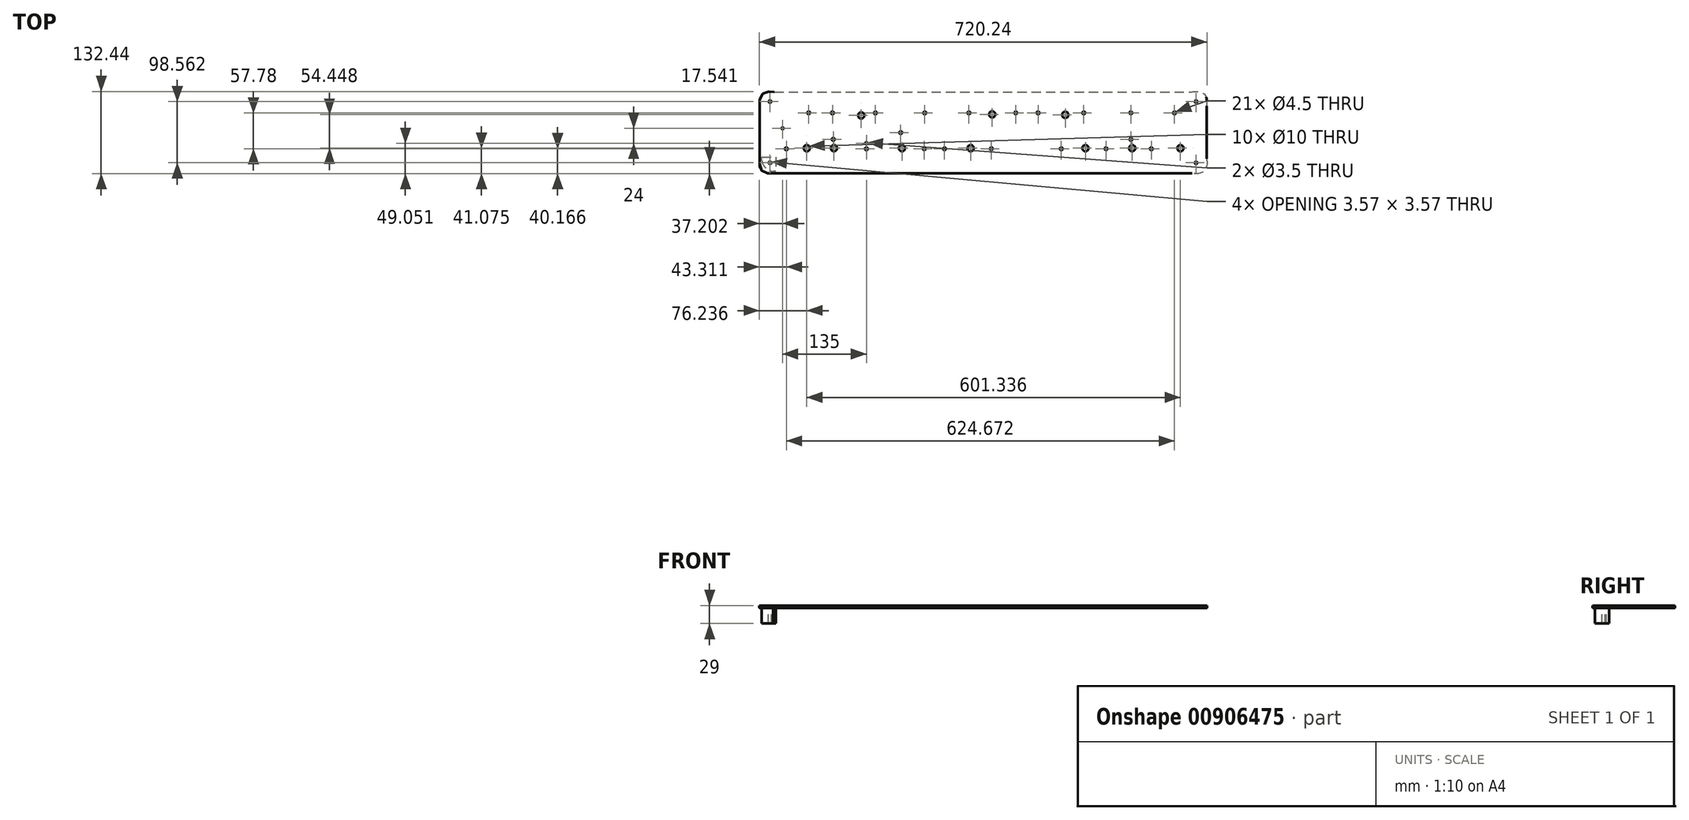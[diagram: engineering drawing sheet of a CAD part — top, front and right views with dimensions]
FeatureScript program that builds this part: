
annotation { "Feature Type Name" : "Feature", "Feature Type Description" : "" }
export const myFeature = defineFeature(function(context is Context, id is Id, definition is map)
    precondition{}
    {
        {
            var Q0;
            Q0=qCreatedBy(makeId("Top.planeOp"),FACE);
            var sketch = newSketch(context, id + "F0", { "sketchPlane" : qUnion([Q0])});
            skFitSpline(sketch, "E0", {"points": [v(336.08, -65.5) * mm, v(336.08, -65.5) * mm, v(336.08, -65.5) * mm, v(333.9, -65.5) * mm, v(-335.86, -65.5) * mm, v(-336.08, -65.5) * mm, v(-336.08, -65.5) * mm, v(-349.03, -65.5) * mm, v(-359.52, -55) * mm, v(-359.52, -42.07) * mm, v(-359.52, -42.06) * mm, v(-359.52, -42.04) * mm, v(-359.52, 42.04) * mm, v(-359.52, 42.06) * mm, v(-359.52, 42.07) * mm, v(-359.51, 55.02) * mm, v(-349.02, 65.5) * mm, v(-336.08, 65.5) * mm]});
            skFitSpline(sketch, "E1", {"points": [v(-336.08, 65.5) * mm, v(-336.08, 65.5) * mm, v(-336.08, 65.5) * mm, v(-333.9, 65.5) * mm, v(335.86, 65.5) * mm, v(336.08, 65.5) * mm, v(336.08, 65.5) * mm, v(349.03, 65.5) * mm, v(359.52, 55) * mm, v(359.52, 42.07) * mm, v(359.52, 42.06) * mm, v(359.52, 42.04) * mm, v(359.52, -42.04) * mm, v(359.52, -42.06) * mm, v(359.52, -42.07) * mm, v(359.51, -55.02) * mm, v(349.02, -65.5) * mm, v(336.08, -65.5) * mm]});
            skFitSpline(sketch, "E2", {"points": [v(-341.32, 49.88) * mm, v(-341.32, 48.9) * mm, v(-342.12, 48.1) * mm, v(-343.1, 48.1) * mm, v(-344.09, 48.1) * mm, v(-344.89, 48.9) * mm, v(-344.89, 49.88) * mm, v(-344.89, 50.87) * mm, v(-344.09, 51.67) * mm, v(-343.1, 51.67) * mm, v(-342.12, 51.67) * mm, v(-341.32, 50.87) * mm, v(-341.32, 49.88) * mm]});
            skFitSpline(sketch, "E3", {"points": [v(-341.32, -48.68) * mm, v(-341.32, -49.66) * mm, v(-342.12, -50.46) * mm, v(-343.1, -50.46) * mm, v(-344.09, -50.46) * mm, v(-344.89, -49.66) * mm, v(-344.89, -48.68) * mm, v(-344.89, -47.7) * mm, v(-344.09, -46.9) * mm, v(-343.1, -46.9) * mm, v(-342.12, -46.9) * mm, v(-341.32, -47.7) * mm, v(-341.32, -48.68) * mm]});
            skFitSpline(sketch, "E4", {"points": [v(344.46, 49.88) * mm, v(344.46, 48.9) * mm, v(343.66, 48.1) * mm, v(342.67, 48.1) * mm, v(341.69, 48.1) * mm, v(340.89, 48.9) * mm, v(340.89, 49.88) * mm, v(340.89, 50.87) * mm, v(341.69, 51.67) * mm, v(342.67, 51.67) * mm, v(343.66, 51.67) * mm, v(344.46, 50.87) * mm, v(344.46, 49.88) * mm]});
            skFitSpline(sketch, "E5", {"points": [v(344.46, -48.68) * mm, v(344.46, -49.66) * mm, v(343.66, -50.46) * mm, v(342.67, -50.46) * mm, v(341.69, -50.46) * mm, v(340.89, -49.66) * mm, v(340.89, -48.68) * mm, v(340.89, -47.7) * mm, v(341.69, -46.9) * mm, v(342.67, -46.9) * mm, v(343.66, -46.9) * mm, v(344.46, -47.7) * mm, v(344.46, -48.68) * mm]});
            skCircle(sketch, "E6", {"center": v(-283.88, -25.14) * mm, "radius": 5 * mm});
            skCircle(sketch, "E7", {"center": v(-240.2, -25.14) * mm, "radius": 5 * mm});
            skCircle(sketch, "E8", {"center": v(-20.1, -25.14) * mm, "radius": 5 * mm});
            skCircle(sketch, "E9", {"center": v(164.53, -25.14) * mm, "radius": 5 * mm});
            skCircle(sketch, "E10", {"center": v(239.74, -25.14) * mm, "radius": 5 * mm});
            skCircle(sketch, "E11", {"center": v(-196.36, 27.6) * mm, "radius": 5 * mm});
            skCircle(sketch, "E12", {"center": v(-130.77, -25.14) * mm, "radius": 5 * mm});
            skCircle(sketch, "E13", {"center": v(14.5, 29.3) * mm, "radius": 5 * mm});
            skCircle(sketch, "E14", {"center": v(132.07, 28.46) * mm, "radius": 5 * mm});
            skCircle(sketch, "E15", {"center": v(317.45, -25.14) * mm, "radius": 5 * mm});
            skSolve(sketch);
        }
        {
            var Q0;
            Q0=qCreatedBy(makeId("Top.planeOp"),FACE);
            var sketch = newSketch(context, id + "F1", { "sketchPlane" : qUnion([Q0])});
            skLineSegment(sketch, "E16", {"start": v(-330.73, -38.95) * mm, "end": v(-330.73, 5.14) * mm});
            skLineSegment(sketch, "E17", {"start": v(-330.73, 5.14) * mm, "end": v(-293.42, 5.14) * mm});
            skLineSegment(sketch, "E18", {"start": v(-293.42, 5.14) * mm, "end": v(-293.42, -11.79) * mm});
            skLineSegment(sketch, "E19", {"start": v(-293.42, -11.79) * mm, "end": v(-296.81, -15.18) * mm});
            skLineSegment(sketch, "E20", {"start": v(-296.81, -15.18) * mm, "end": v(-296.81, -18.63) * mm});
            skLineSegment(sketch, "E21", {"start": v(-296.81, -18.63) * mm, "end": v(-293.42, -22) * mm});
            skLineSegment(sketch, "E22", {"start": v(-293.42, -22) * mm, "end": v(-293.42, -38.95) * mm});
            skLineSegment(sketch, "E23", {"start": v(-293.42, -38.95) * mm, "end": v(-330.73, -38.95) * mm});
            skLineSegment(sketch, "E24", {"start": v(-317.16, -5.03) * mm, "end": v(-317.16, -11.82) * mm});
            skLineSegment(sketch, "E25", {"start": v(-317.16, -11.82) * mm, "end": v(-313.83, -11.82) * mm});
            skLineSegment(sketch, "E26", {"start": v(-313.83, -11.82) * mm, "end": v(-310.37, -8.58) * mm});
            skLineSegment(sketch, "E27", {"start": v(-310.37, -8.58) * mm, "end": v(-310.37, -5.03) * mm});
            skLineSegment(sketch, "E28", {"start": v(-310.37, -5.03) * mm, "end": v(-313.86, -5.03) * mm});
            skLineSegment(sketch, "E29", {"start": v(-313.86, -5.03) * mm, "end": v(-317.16, -5.03) * mm});
            skLineSegment(sketch, "E30", {"start": v(-317.16, -22) * mm, "end": v(-317.16, -28.78) * mm});
            skLineSegment(sketch, "E31", {"start": v(-317.16, -28.78) * mm, "end": v(-313.81, -28.78) * mm});
            skLineSegment(sketch, "E32", {"start": v(-313.81, -28.78) * mm, "end": v(-310.37, -25.37) * mm});
            skLineSegment(sketch, "E33", {"start": v(-310.37, -25.37) * mm, "end": v(-310.37, -22) * mm});
            skLineSegment(sketch, "E34", {"start": v(-310.37, -22) * mm, "end": v(-313.74, -22) * mm});
            skLineSegment(sketch, "E35", {"start": v(-313.74, -22) * mm, "end": v(-317.16, -22) * mm});
            skLineSegment(sketch, "E36", {"start": v(-289.9, 5.14) * mm, "end": v(-272.94, 5.14) * mm});
            skLineSegment(sketch, "E37", {"start": v(-272.94, 5.14) * mm, "end": v(-272.94, -38.95) * mm});
            skLineSegment(sketch, "E38", {"start": v(-272.94, -38.95) * mm, "end": v(-289.9, -38.95) * mm});
            skLineSegment(sketch, "E39", {"start": v(-289.9, -38.95) * mm, "end": v(-289.9, 5.14) * mm});
            skLineSegment(sketch, "E40", {"start": v(-259.27, -38.95) * mm, "end": v(-259.27, -15.2) * mm});
            skLineSegment(sketch, "E41", {"start": v(-259.27, -15.2) * mm, "end": v(-269.43, -15.2) * mm});
            skLineSegment(sketch, "E42", {"start": v(-269.43, -15.2) * mm, "end": v(-269.43, 5.14) * mm});
            skLineSegment(sketch, "E43", {"start": v(-269.43, 5.14) * mm, "end": v(-232.12, 5.14) * mm});
            skLineSegment(sketch, "E44", {"start": v(-232.12, 5.14) * mm, "end": v(-232.12, -15.2) * mm});
            skLineSegment(sketch, "E45", {"start": v(-232.12, -15.2) * mm, "end": v(-242.28, -15.2) * mm});
            skLineSegment(sketch, "E46", {"start": v(-242.28, -15.2) * mm, "end": v(-242.28, -38.95) * mm});
            skLineSegment(sketch, "E47", {"start": v(-242.28, -38.95) * mm, "end": v(-259.27, -38.95) * mm});
            skLineSegment(sketch, "E48", {"start": v(-228.6, -38.95) * mm, "end": v(-228.6, 5.14) * mm});
            skLineSegment(sketch, "E49", {"start": v(-228.6, 5.14) * mm, "end": v(-191.3, 5.14) * mm});
            skLineSegment(sketch, "E50", {"start": v(-191.3, 5.14) * mm, "end": v(-191.3, -18.6) * mm});
            skLineSegment(sketch, "E51", {"start": v(-191.3, -18.6) * mm, "end": v(-194.73, -22) * mm});
            skLineSegment(sketch, "E52", {"start": v(-194.73, -22) * mm, "end": v(-191.3, -25.39) * mm});
            skLineSegment(sketch, "E53", {"start": v(-191.3, -25.39) * mm, "end": v(-191.3, -38.95) * mm});
            skLineSegment(sketch, "E54", {"start": v(-191.3, -38.95) * mm, "end": v(-208.28, -38.95) * mm});
            skLineSegment(sketch, "E55", {"start": v(-208.28, -38.95) * mm, "end": v(-208.28, -22.04) * mm});
            skLineSegment(sketch, "E56", {"start": v(-208.28, -22.04) * mm, "end": v(-211.67, -22.04) * mm});
            skLineSegment(sketch, "E57", {"start": v(-211.67, -22.04) * mm, "end": v(-211.67, -38.95) * mm});
            skLineSegment(sketch, "E58", {"start": v(-211.67, -38.95) * mm, "end": v(-228.6, -38.95) * mm});
            skLineSegment(sketch, "E59", {"start": v(-215.06, -5.03) * mm, "end": v(-215.06, -11.82) * mm});
            skLineSegment(sketch, "E60", {"start": v(-215.06, -11.82) * mm, "end": v(-211.71, -11.82) * mm});
            skLineSegment(sketch, "E61", {"start": v(-211.71, -11.82) * mm, "end": v(-208.28, -8.41) * mm});
            skLineSegment(sketch, "E62", {"start": v(-208.28, -8.41) * mm, "end": v(-208.28, -5.03) * mm});
            skLineSegment(sketch, "E63", {"start": v(-208.28, -5.03) * mm, "end": v(-211.64, -5.03) * mm});
            skLineSegment(sketch, "E64", {"start": v(-211.64, -5.03) * mm, "end": v(-215.06, -5.03) * mm});
            skLineSegment(sketch, "E65", {"start": v(-187.79, -38.95) * mm, "end": v(-187.79, 5.14) * mm});
            skLineSegment(sketch, "E66", {"start": v(-187.79, 5.14) * mm, "end": v(-150.47, 5.14) * mm});
            skLineSegment(sketch, "E67", {"start": v(-150.47, 5.14) * mm, "end": v(-150.47, -38.95) * mm});
            skLineSegment(sketch, "E68", {"start": v(-150.47, -38.95) * mm, "end": v(-187.79, -38.95) * mm});
            skLineSegment(sketch, "E69", {"start": v(-174.17, -5.15) * mm, "end": v(-174.17, -25.5) * mm});
            skLineSegment(sketch, "E70", {"start": v(-174.17, -25.5) * mm, "end": v(-167.39, -25.5) * mm});
            skLineSegment(sketch, "E71", {"start": v(-167.39, -25.5) * mm, "end": v(-167.39, -5.15) * mm});
            skLineSegment(sketch, "E72", {"start": v(-167.39, -5.15) * mm, "end": v(-174.17, -5.15) * mm});
            skLineSegment(sketch, "E73", {"start": v(-146.96, -38.95) * mm, "end": v(-146.96, 5.14) * mm});
            skLineSegment(sketch, "E74", {"start": v(-146.96, 5.14) * mm, "end": v(-109.65, 5.14) * mm});
            skLineSegment(sketch, "E75", {"start": v(-109.65, 5.14) * mm, "end": v(-109.65, -18.83) * mm});
            skLineSegment(sketch, "E76", {"start": v(-109.65, -18.83) * mm, "end": v(-112.94, -22.03) * mm});
            skLineSegment(sketch, "E77", {"start": v(-112.94, -22.03) * mm, "end": v(-123.2, -22.03) * mm});
            skLineSegment(sketch, "E78", {"start": v(-123.2, -22.03) * mm, "end": v(-123.2, -38.95) * mm});
            skLineSegment(sketch, "E79", {"start": v(-123.2, -38.95) * mm, "end": v(-146.96, -38.95) * mm});
            skLineSegment(sketch, "E80", {"start": v(-133.4, -5.03) * mm, "end": v(-133.4, -11.82) * mm});
            skLineSegment(sketch, "E81", {"start": v(-133.4, -11.82) * mm, "end": v(-130.05, -11.82) * mm});
            skLineSegment(sketch, "E82", {"start": v(-130.05, -11.82) * mm, "end": v(-126.62, -8.41) * mm});
            skLineSegment(sketch, "E83", {"start": v(-126.62, -8.41) * mm, "end": v(-126.62, -5.03) * mm});
            skLineSegment(sketch, "E84", {"start": v(-126.62, -5.03) * mm, "end": v(-129.98, -5.03) * mm});
            skLineSegment(sketch, "E85", {"start": v(-129.98, -5.03) * mm, "end": v(-133.4, -5.03) * mm});
            skLineSegment(sketch, "E86", {"start": v(-106.14, -38.95) * mm, "end": v(-106.14, 5.14) * mm});
            skLineSegment(sketch, "E87", {"start": v(-106.14, 5.14) * mm, "end": v(-68.83, 5.14) * mm});
            skLineSegment(sketch, "E88", {"start": v(-68.83, 5.14) * mm, "end": v(-68.83, -38.95) * mm});
            skLineSegment(sketch, "E89", {"start": v(-68.83, -38.95) * mm, "end": v(-106.14, -38.95) * mm});
            skLineSegment(sketch, "E90", {"start": v(-92.57, -5.15) * mm, "end": v(-92.57, -25.5) * mm});
            skLineSegment(sketch, "E91", {"start": v(-92.57, -25.5) * mm, "end": v(-85.79, -25.5) * mm});
            skLineSegment(sketch, "E92", {"start": v(-85.79, -25.5) * mm, "end": v(-85.79, -5.15) * mm});
            skLineSegment(sketch, "E93", {"start": v(-85.79, -5.15) * mm, "end": v(-92.57, -5.15) * mm});
            skLineSegment(sketch, "E94", {"start": v(-65.32, -38.95) * mm, "end": v(-65.32, 5.14) * mm});
            skLineSegment(sketch, "E95", {"start": v(-65.32, 5.14) * mm, "end": v(-48.24, 5.14) * mm});
            skLineSegment(sketch, "E96", {"start": v(-48.24, 5.14) * mm, "end": v(-48.24, -25.4) * mm});
            skLineSegment(sketch, "E97", {"start": v(-48.24, -25.4) * mm, "end": v(-28, -25.4) * mm});
            skLineSegment(sketch, "E98", {"start": v(-28, -25.4) * mm, "end": v(-28, -38.95) * mm});
            skLineSegment(sketch, "E99", {"start": v(-28, -38.95) * mm, "end": v(-65.32, -38.95) * mm});
            skLineSegment(sketch, "E100", {"start": v(-24.5, 5.14) * mm, "end": v(-7.53, 5.14) * mm});
            skLineSegment(sketch, "E101", {"start": v(-7.53, 5.14) * mm, "end": v(-7.53, -38.95) * mm});
            skLineSegment(sketch, "E102", {"start": v(-7.53, -38.95) * mm, "end": v(-24.5, -38.95) * mm});
            skLineSegment(sketch, "E103", {"start": v(-24.5, -38.95) * mm, "end": v(-24.5, 5.14) * mm});
            skLineSegment(sketch, "E104", {"start": v(-4.02, -38.95) * mm, "end": v(-4.02, -25.4) * mm});
            skLineSegment(sketch, "E105", {"start": v(-4.02, -25.4) * mm, "end": v(19.67, -25.4) * mm});
            skLineSegment(sketch, "E106", {"start": v(19.67, -25.4) * mm, "end": v(19.67, -22.03) * mm});
            skLineSegment(sketch, "E107", {"start": v(19.67, -22.03) * mm, "end": v(-4.02, -22.03) * mm});
            skLineSegment(sketch, "E108", {"start": v(-4.02, -22.03) * mm, "end": v(-4.02, 5.14) * mm});
            skLineSegment(sketch, "E109", {"start": v(-4.02, 5.14) * mm, "end": v(33.29, 5.14) * mm});
            skLineSegment(sketch, "E110", {"start": v(33.29, 5.14) * mm, "end": v(33.29, -8.43) * mm});
            skLineSegment(sketch, "E111", {"start": v(33.29, -8.43) * mm, "end": v(9.54, -8.43) * mm});
            skLineSegment(sketch, "E112", {"start": v(9.54, -8.43) * mm, "end": v(9.54, -11.82) * mm});
            skLineSegment(sketch, "E113", {"start": v(9.54, -11.82) * mm, "end": v(33.29, -11.82) * mm});
            skLineSegment(sketch, "E114", {"start": v(33.29, -11.82) * mm, "end": v(33.29, -38.95) * mm});
            skLineSegment(sketch, "E115", {"start": v(33.29, -38.95) * mm, "end": v(-4.02, -38.95) * mm});
            skFitSpline(sketch, "E116", {"points": [v(36.9, -53.5) * mm, v(36.89, -53.5) * mm, v(36.89, -53.5) * mm, v(35.69, -53.5) * mm, v(-333.72, -53.5) * mm, v(-333.84, -53.5) * mm, v(-333.84, -53.5) * mm, v(-340.98, -53.5) * mm, v(-346.77, -47.71) * mm, v(-346.77, -40.57) * mm, v(-346.77, -40.57) * mm, v(-346.77, -40.56) * mm, v(-346.77, 5.82) * mm, v(-346.77, 5.83) * mm, v(-346.77, 5.83) * mm, v(-346.76, 12.97) * mm, v(-340.98, 18.76) * mm, v(-333.84, 18.76) * mm]});
            skFitSpline(sketch, "E117", {"points": [v(-333.84, 18.76) * mm, v(-333.84, 18.76) * mm, v(-333.84, 18.76) * mm, v(-332.63, 18.76) * mm, v(36.77, 18.76) * mm, v(36.9, 18.76) * mm, v(36.9, 18.76) * mm, v(44.03, 18.75) * mm, v(49.82, 12.97) * mm, v(49.82, 5.83) * mm, v(49.82, 5.83) * mm, v(49.82, 5.81) * mm, v(49.82, -40.56) * mm, v(49.82, -40.57) * mm, v(49.82, -40.58) * mm, v(49.82, -47.72) * mm, v(44.03, -53.5) * mm, v(36.9, -53.5) * mm]});
            skFitSpline(sketch, "E118", {"points": [v(-336.73, 10.14) * mm, v(-336.73, 9.6) * mm, v(-337.17, 9.16) * mm, v(-337.71, 9.16) * mm, v(-338.26, 9.16) * mm, v(-338.7, 9.6) * mm, v(-338.7, 10.14) * mm, v(-338.7, 10.68) * mm, v(-338.26, 11.13) * mm, v(-337.71, 11.13) * mm, v(-337.17, 11.13) * mm, v(-336.73, 10.68) * mm, v(-336.73, 10.14) * mm]});
            skFitSpline(sketch, "E119", {"points": [v(-336.73, -44.22) * mm, v(-336.73, -44.76) * mm, v(-337.17, -45.2) * mm, v(-337.71, -45.2) * mm, v(-338.26, -45.2) * mm, v(-338.7, -44.76) * mm, v(-338.7, -44.22) * mm, v(-338.7, -43.68) * mm, v(-338.26, -43.24) * mm, v(-337.71, -43.24) * mm, v(-337.17, -43.24) * mm, v(-336.73, -43.68) * mm, v(-336.73, -44.22) * mm]});
            skFitSpline(sketch, "E120", {"points": [v(41.51, 10.14) * mm, v(41.51, 9.6) * mm, v(41.07, 9.16) * mm, v(40.53, 9.16) * mm, v(39.98, 9.16) * mm, v(39.54, 9.6) * mm, v(39.54, 10.14) * mm, v(39.54, 10.68) * mm, v(39.98, 11.13) * mm, v(40.53, 11.13) * mm, v(41.07, 11.13) * mm, v(41.51, 10.68) * mm, v(41.51, 10.14) * mm]});
            skFitSpline(sketch, "E121", {"points": [v(41.51, -44.22) * mm, v(41.51, -44.76) * mm, v(41.07, -45.2) * mm, v(40.53, -45.2) * mm, v(39.98, -45.2) * mm, v(39.54, -44.76) * mm, v(39.54, -44.22) * mm, v(39.54, -43.68) * mm, v(39.98, -43.24) * mm, v(40.53, -43.24) * mm, v(41.07, -43.24) * mm, v(41.51, -43.68) * mm, v(41.51, -44.22) * mm]});
            skSolve(sketch);
        }
        {
            var Q0;
            Q0 = qConstructionFilter(qBodyType(qCreatedBy(id + "F1" ,EDGE), BodyType.WIRE), ConstructionObject.NO);
            extrude(context, id + "F2", {"bodyType" : ToolBodyType.SURFACE, "surfaceEntities" : qUnion([Q0]), "depth" : 25 * mm, "offsetDistance" : 25 * mm});
        }
        {
            var Q0;
            Q0=makeQuery(id+"F2.opExtrude","SWEPT_BODY",BODY,{"disambiguationData":[OSD([sQuery(id+"F1.wireOp",EDGE,"E23")])]});
            var Q1;
            Q1=makeQuery(id+"F2.opExtrude","SWEPT_BODY",BODY,{"disambiguationData":[OSD([sQuery(id+"F1.wireOp",EDGE,"E28"),sQuery(id+"F1.wireOp",EDGE,"E29")])]});
            var Q2;
            Q2=makeQuery(id+"F2.opExtrude","SWEPT_BODY",BODY,{"disambiguationData":[OSD([sQuery(id+"F1.wireOp",EDGE,"E34"),sQuery(id+"F1.wireOp",EDGE,"E35")])]});
            var Q3;
            Q3=makeQuery(id+"F2.opExtrude","SWEPT_BODY",BODY,{"disambiguationData":[OSD([sQuery(id+"F1.wireOp",EDGE,"E39")])]});
            var Q4;
            Q4=makeQuery(id+"F2.opExtrude","SWEPT_BODY",BODY,{"disambiguationData":[OSD([sQuery(id+"F1.wireOp",EDGE,"E47")])]});
            var Q5;
            Q5=makeQuery(id+"F2.opExtrude","SWEPT_BODY",BODY,{"disambiguationData":[OSD([sQuery(id+"F1.wireOp",EDGE,"E58")])]});
            var Q6;
            Q6=makeQuery(id+"F2.opExtrude","SWEPT_BODY",BODY,{"disambiguationData":[OSD([sQuery(id+"F1.wireOp",EDGE,"E63"),sQuery(id+"F1.wireOp",EDGE,"E64")])]});
            var Q7;
            Q7=makeQuery(id+"F2.opExtrude","SWEPT_BODY",BODY,{"disambiguationData":[OSD([sQuery(id+"F1.wireOp",EDGE,"E68")])]});
            var Q8;
            Q8=makeQuery(id+"F2.opExtrude","SWEPT_BODY",BODY,{"disambiguationData":[OSD([sQuery(id+"F1.wireOp",EDGE,"E72")])]});
            var Q9;
            Q9=makeQuery(id+"F2.opExtrude","SWEPT_BODY",BODY,{"disambiguationData":[OSD([sQuery(id+"F1.wireOp",EDGE,"E79")])]});
            var Q10;
            Q10=makeQuery(id+"F2.opExtrude","SWEPT_BODY",BODY,{"disambiguationData":[OSD([sQuery(id+"F1.wireOp",EDGE,"E84"),sQuery(id+"F1.wireOp",EDGE,"E85")])]});
            var Q11;
            Q11=makeQuery(id+"F2.opExtrude","SWEPT_BODY",BODY,{"disambiguationData":[OSD([sQuery(id+"F1.wireOp",EDGE,"E89")])]});
            var Q12;
            Q12=makeQuery(id+"F2.opExtrude","SWEPT_BODY",BODY,{"disambiguationData":[OSD([sQuery(id+"F1.wireOp",EDGE,"E93")])]});
            var Q13;
            Q13=makeQuery(id+"F2.opExtrude","SWEPT_BODY",BODY,{"disambiguationData":[OSD([sQuery(id+"F1.wireOp",EDGE,"E99")])]});
            var Q14;
            Q14=makeQuery(id+"F2.opExtrude","SWEPT_BODY",BODY,{"disambiguationData":[OSD([sQuery(id+"F1.wireOp",EDGE,"E103")])]});
            var Q15;
            Q15=makeQuery(id+"F2.opExtrude","SWEPT_BODY",BODY,{"disambiguationData":[OSD([sQuery(id+"F1.wireOp",EDGE,"E115")])]});
            var Q16;
            Q16=makeQuery(id+"F2.opExtrude","SWEPT_BODY",BODY,{"disambiguationData":[OSD([sQuery(id+"F1.wireOp",EDGE,"E117")])]});
            var Q17;
            Q17=makeQuery(id+"F2.opExtrude","SWEPT_BODY",BODY,{"disambiguationData":[OSD([sQuery(id+"F1.wireOp",EDGE,"E118")])]});
            var Q18;
            Q18=makeQuery(id+"F2.opExtrude","SWEPT_BODY",BODY,{"disambiguationData":[OSD([sQuery(id+"F1.wireOp",EDGE,"E119")])]});
            var Q19;
            Q19=makeQuery(id+"F2.opExtrude","SWEPT_BODY",BODY,{"disambiguationData":[OSD([sQuery(id+"F1.wireOp",EDGE,"E120")])]});
            var Q20;
            Q20=makeQuery(id+"F2.opExtrude","SWEPT_BODY",BODY,{"disambiguationData":[OSD([sQuery(id+"F1.wireOp",EDGE,"E121")])]});
            var Q21;
            Q21=makeQuery(id+"F2.opExtrude","CAP_VERTEX",VERTEX,{"disambiguationData":[OSD([sQuery(id+"F1.wireOp",VERTEX,"E23.end")])],"isStart":true});
            transform(context, id + "F3", {"entities" : qUnion([Q0, Q1, Q2, Q3, Q4, Q5, Q6, Q7, Q8, Q9, Q10, Q11, Q12, Q13, Q14, Q15, Q16, Q17, Q18, Q19, Q20]), "transformType" : TransformType.SCALE_UNIFORMLY, "scale" : 1.81, "scalePoint" : qUnion([Q21]), "makeCopy" : false});
        }
        {
            var Q0;
            Q0 = qSketchRegion(id + "F0", true);
            extrude(context, id + "F4", {"entities" : qUnion([Q0]), "oppositeDirection" : true, "depth" : 4 * mm, "offsetDistance" : 25 * mm});
        }
        {
            var Q0;
            Q0=makeQuery(id+"F0.imprint","IMPRINT",FACE,{"disambiguationData":[TD([[makeQuery(id+"F0.imprint","IMPRINT",EDGE,{"derivedFrom":sQuery(id+"F0.wireOp",EDGE,"E0")}),-1.0]])]});
            var sketch = newSketch(context, id + "F5", { "sketchPlane" : qUnion([Q0])});
            skCircle(sketch, "E122", {"center": v(-280.9, 31.73) * mm, "radius": 2.25 * mm});
            skCircle(sketch, "E123", {"center": v(-242.59, 31.73) * mm, "radius": 2.25 * mm});
            skCircle(sketch, "E124", {"center": v(-173.53, 31.73) * mm, "radius": 2.25 * mm});
            skCircle(sketch, "E125", {"center": v(-94.1, 31.73) * mm, "radius": 2.25 * mm});
            skCircle(sketch, "E126", {"center": v(-23.04, 31.73) * mm, "radius": 2.25 * mm});
            skCircle(sketch, "E127", {"center": v(52.4, 31.73) * mm, "radius": 2.25 * mm});
            skCircle(sketch, "E128", {"center": v(88.33, 31.73) * mm, "radius": 2.25 * mm});
            skCircle(sketch, "E129", {"center": v(161.78, 31.73) * mm, "radius": 2.25 * mm});
            skCircle(sketch, "E130", {"center": v(237.7, 31.73) * mm, "radius": 2.25 * mm});
            skCircle(sketch, "E131", {"center": v(307.86, 31.73) * mm, "radius": 2.25 * mm});
            skCircle(sketch, "E132", {"center": v(270.6, -26.05) * mm, "radius": 2.25 * mm});
            skCircle(sketch, "E133", {"center": v(237.7, -10.95) * mm, "radius": 2.25 * mm});
            skCircle(sketch, "E134", {"center": v(197.76, -26.05) * mm, "radius": 2.25 * mm});
            skCircle(sketch, "E135", {"center": v(125.6, -26.05) * mm, "radius": 2.25 * mm});
            skCircle(sketch, "E136", {"center": v(13.15, -26.05) * mm, "radius": 2.25 * mm});
            skCircle(sketch, "E137", {"center": v(-62.38, -26.05) * mm, "radius": 2.25 * mm});
            skCircle(sketch, "E138", {"center": v(-94.94, -26.05) * mm, "radius": 2.25 * mm});
            skCircle(sketch, "E139", {"center": v(-132.87, 0) * mm, "radius": 2.25 * mm});
            skCircle(sketch, "E140", {"center": v(-187.92, -26.05) * mm, "radius": 2.25 * mm});
            skCircle(sketch, "E141", {"center": v(-241.29, -10.95) * mm, "radius": 2.25 * mm});
            skCircle(sketch, "E142", {"center": v(-316.8, -26.05) * mm, "radius": 2.25 * mm});
            skCircle(sketch, "E143", {"center": v(-322.92, 6.83) * mm, "radius": 1.75 * mm});
            skCircle(sketch, "E144", {"center": v(-187.92, -17.17) * mm, "radius": 1.75 * mm});
            skSolve(sketch);
        }
        {
            var Q0;
            Q0 = qSketchRegion(id + "F5", true);
            extrude(context, id + "F6", {"entities" : qUnion([Q0]), "operationType" : NewBodyOperationType.REMOVE, "oppositeDirection" : true, "depth" : 25 * mm, "offsetDistance" : 25 * mm});
        }
        {
            var Q0;
            Q0=makeQuery(id+"F4.opExtrude","CAP_FACE",FACE,{"disambiguationData":[OSD([sQuery(id+"F0.wireOp",EDGE,"E0"),sQuery(id+"F0.wireOp",EDGE,"E1"),sQuery(id+"F0.wireOp",EDGE,"E2"),sQuery(id+"F0.wireOp",EDGE,"E3"),sQuery(id+"F0.wireOp",EDGE,"E4"),sQuery(id+"F0.wireOp",EDGE,"E5"),sQuery(id+"F0.wireOp",EDGE,"E6"),sQuery(id+"F0.wireOp",EDGE,"E7"),sQuery(id+"F0.wireOp",EDGE,"E8"),sQuery(id+"F0.wireOp",EDGE,"E9"),sQuery(id+"F0.wireOp",EDGE,"E10"),sQuery(id+"F0.wireOp",EDGE,"E11"),sQuery(id+"F0.wireOp",EDGE,"E12"),sQuery(id+"F0.wireOp",EDGE,"E13"),sQuery(id+"F0.wireOp",EDGE,"E14"),sQuery(id+"F0.wireOp",EDGE,"E15")])],"isStart":false});
            var sketch = newSketch(context, id + "F7", { "sketchPlane" : qUnion([Q0])});
            skCircle(sketch, "E145", {"center": v(-343.1, 48.65) * mm, "radius": 2.64 * mm});
            skArc(sketch, "E146", {"start": v(-338.52, 65.38) * mm, "mid": v(-352.56, 58.54) * mm, "end": v(-359.4, 44.5) * mm, "construction": true});
            skLineSegment(sketch, "E147", {"start": v(-359.4, 44.5) * mm, "end": v(-338.52, 44.5) * mm, "construction": true});
            skLineSegment(sketch, "E148", {"start": v(-338.52, 44.5) * mm, "end": v(-338.52, 65.38) * mm, "construction": true});
            skLineSegment(sketch, "E149", {"start": v(-359.4, 44.5) * mm, "end": v(-359.52, 36.5) * mm, "construction": true});
            skLineSegment(sketch, "E150", {"start": v(-359.52, 36.5) * mm, "end": v(-330.52, 36.5) * mm, "construction": true});
            skLineSegment(sketch, "E151", {"start": v(-330.52, 36.5) * mm, "end": v(-330.52, 65.5) * mm, "construction": true});
            skLineSegment(sketch, "E152", {"start": v(-330.52, 65.5) * mm, "end": v(-338.52, 65.38) * mm, "construction": true});
            skLineSegment(sketch, "E153.0", {"start": v(-356.47, 39.5) * mm, "end": v(-333.52, 39.5) * mm});
            skLineSegment(sketch, "E153.1", {"start": v(-356.4, 44.3) * mm, "end": v(-356.47, 39.5) * mm});
            skLineSegment(sketch, "E153.2", {"start": v(-333.52, 39.5) * mm, "end": v(-333.52, 62.46) * mm});
            skLineSegment(sketch, "E153.3", {"start": v(-333.52, 62.46) * mm, "end": v(-338.3, 62.38) * mm});
            skArc(sketch, "E153.4", {"start": v(-338.3, 62.38) * mm, "mid": v(-350.44, 56.42) * mm, "end": v(-356.4, 44.3) * mm});
            skSolve(sketch);
        }
        {
            var Q0;
            Q0 = qSketchRegion(id + "F7", true);
            extrude(context, id + "F8", {"entities" : qUnion([Q0]), "depth" : 25 * mm, "offsetDistance" : 25 * mm});
        }
    });
